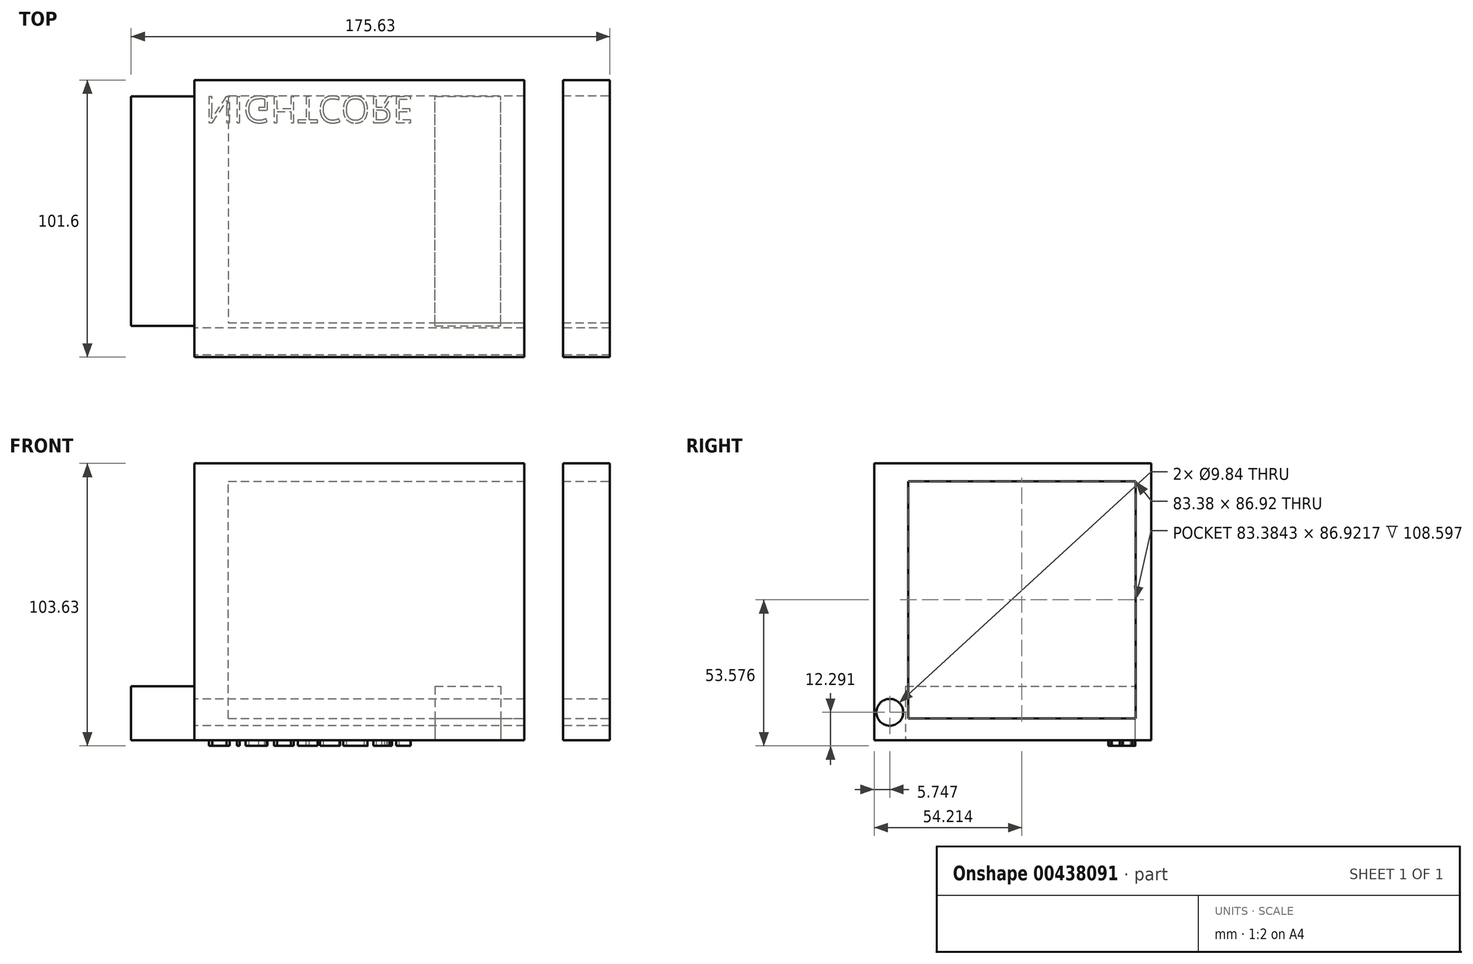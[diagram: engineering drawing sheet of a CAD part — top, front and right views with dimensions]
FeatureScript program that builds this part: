
annotation { "Feature Type Name" : "Feature", "Feature Type Description" : "" }
export const myFeature = defineFeature(function(context is Context, id is Id, definition is map)
    precondition{}
    {
        {
            var Q0;
            Q0=qCreatedBy(makeId("Top.planeOp"),FACE);
            var sketch = newSketch(context, id + "F0", { "sketchPlane" : qUnion([Q0])});
            skLineSegment(sketch, "E0.bottom", {"start": v(-70.16, 123.67) * mm, "end": v(82.24, 123.67) * mm});
            skLineSegment(sketch, "E0.top", {"start": v(-70.16, 22.07) * mm, "end": v(82.24, 22.07) * mm});
            skLineSegment(sketch, "E0.left", {"start": v(-70.16, 123.67) * mm, "end": v(-70.16, 22.07) * mm});
            skLineSegment(sketch, "E0.right", {"start": v(82.24, 123.67) * mm, "end": v(82.24, 22.07) * mm});
            skLineSegment(sketch, "E1.bottom", {"start": v(50.89, 123.67) * mm, "end": v(65.05, 123.67) * mm});
            skLineSegment(sketch, "E1.top", {"start": v(50.89, 22.07) * mm, "end": v(65.05, 22.07) * mm});
            skLineSegment(sketch, "E1.left", {"start": v(50.89, 123.67) * mm, "end": v(50.89, 22.07) * mm});
            skLineSegment(sketch, "E1.right", {"start": v(65.05, 123.67) * mm, "end": v(65.05, 22.07) * mm});
            skSolve(sketch);
        }
        {
            var Q0;
            {var subQ0=sQuery(id+"F0.wireOp",EDGE,"E0.right");Q0=makeQuery(id+"F0.imprint","IMPRINT",FACE,{"disambiguationData":[TD([[makeQuery(id+"F0.imprint","IMPRINT",EDGE,{"derivedFrom":subQ0}),-1.0]])]});}
            var Q1;
            {var subQ0=sQuery(id+"F0.wireOp",EDGE,"E0.left");Q1=makeQuery(id+"F0.imprint","IMPRINT",FACE,{"disambiguationData":[TD([[makeQuery(id+"F0.imprint","IMPRINT",EDGE,{"derivedFrom":subQ0}),1.0]])]});}
            var Q2;
            Q2=makeQuery(id+"F0.imprint","IMPRINT",FACE,{"disambiguationData":[TD([[makeQuery(id+"F0.imprint","IMPRINT",EDGE,{"derivedFrom":sQuery(id+"F0.wireOp",EDGE,"E1.bottom")}),-1.0]])]});
            extrude(context, id + "F1", {"entities" : qUnion([Q0, Q1, Q2]), "depth" : 101.6 * mm});
        }
        {
            var Q0;
            Q0=makeQuery(id+"F1.opExtrude","SWEPT_FACE",FACE,{"disambiguationData":[OSD([sQuery(id+"F0.wireOp",EDGE,"E0.left")])]});
            var sketch = newSketch(context, id + "F2", { "sketchPlane" : qUnion([Q0])});
            skCircle(sketch, "E2", {"center": v(-27.82, 10.26) * mm, "radius": 4.92 * mm});
            skSolve(sketch);
        }
        {
            var Q0;
            Q0=makeQuery(id+"F2.imprint","IMPRINT",FACE,{"disambiguationData":[TD([[makeQuery(id+"F2.imprint","IMPRINT",EDGE,{"derivedFrom":sQuery(id+"F2.wireOp",EDGE,"E2")}),1.0]])]});
            extrude(context, id + "F3", {"entities" : qUnion([Q0]), "operationType" : NewBodyOperationType.REMOVE, "oppositeDirection" : true, "depth" : 164.85 * mm});
        }
        {
            var Q0;
            Q0=makeQuery(id+"F1.opExtrude","CAP_FACE",FACE,{"disambiguationData":[OSD([sQuery(id+"F0.wireOp",EDGE,"E0.bottom"),sQuery(id+"F0.wireOp",EDGE,"E0.top"),sQuery(id+"F0.wireOp",EDGE,"E0.left"),sQuery(id+"F0.wireOp",EDGE,"E0.right"),sQuery(id+"F0.wireOp",EDGE,"E1.bottom"),sQuery(id+"F0.wireOp",EDGE,"E1.top")])],"isStart":true});
            var sketch = newSketch(context, id + "F4", { "sketchPlane" : qUnion([Q0])});
            skLineSegment(sketch, "E3.bottom", {"start": v(18.12, -33.55) * mm, "end": v(42.28, -33.55) * mm});
            skLineSegment(sketch, "E3.top", {"start": v(18.12, -117.72) * mm, "end": v(42.28, -117.72) * mm});
            skLineSegment(sketch, "E3.left", {"start": v(18.12, -33.55) * mm, "end": v(18.12, -117.72) * mm});
            skLineSegment(sketch, "E3.right", {"start": v(42.28, -33.55) * mm, "end": v(42.28, -117.72) * mm});
            skSolve(sketch);
        }
        {
            var Q0;
            Q0=makeQuery(id+"F4.imprint","IMPRINT",FACE,{"disambiguationData":[TD([[makeQuery(id+"F4.imprint","IMPRINT",EDGE,{"derivedFrom":sQuery(id+"F4.wireOp",EDGE,"E3.bottom")}),-1.0]])]});
            extrude(context, id + "F5", {"entities" : qUnion([Q0]), "operationType" : NewBodyOperationType.REMOVE, "oppositeDirection" : true, "depth" : 19.8 * mm});
        }
        {
            var Q0;
            Q0=makeQuery(id+"F1.opExtrude","CAP_FACE",FACE,{"disambiguationData":[OSD([sQuery(id+"F0.wireOp",EDGE,"E0.bottom"),sQuery(id+"F0.wireOp",EDGE,"E0.top"),sQuery(id+"F0.wireOp",EDGE,"E0.left"),sQuery(id+"F0.wireOp",EDGE,"E0.right"),sQuery(id+"F0.wireOp",EDGE,"E1.bottom"),sQuery(id+"F0.wireOp",EDGE,"E1.top")])],"isStart":true});
            var sketch = newSketch(context, id + "F6", { "sketchPlane" : qUnion([Q0])});
            skText(sketch, "E4", { "text": "NIGHTCORE", "fontName": "OpenSans-Regular.ttf"});
            const initialGuessF6  = {"E4": [-0.06612, -0.11772, 1, 0, 0.00973]};
            skSetInitialGuess(sketch, initialGuessF6);
            skSolve(sketch);
        }
        {
            var Q0;
            Q0 = qSketchRegion(id + "F6", true);
            extrude(context, id + "F7", {"entities" : qUnion([Q0]), "operationType" : NewBodyOperationType.ADD, "depth" : 2.03 * mm});
        }
        {
            var Q0;
            Q0=makeQuery(id+"F5.boolean.opBoolean","COPY",FACE,{"derivedFrom":makeQuery(id+"F5.opExtrude","SWEPT_FACE",FACE,{"disambiguationData":[OSD([sQuery(id+"F4.wireOp",EDGE,"E3.left")])]})});
            extrude(context, id + "F8", {"entities" : qUnion([Q0]), "operationType" : NewBodyOperationType.ADD, "oppositeDirection" : true, "depth" : 111.5 * mm});
        }
        {
            var Q0;
            Q0=makeQuery(id+"F1.opExtrude","SWEPT_FACE",FACE,{"disambiguationData":[OSD([sQuery(id+"F0.wireOp",EDGE,"E0.right")])]});
            var sketch = newSketch(context, id + "F9", { "sketchPlane" : qUnion([Q0])});
            skLineSegment(sketch, "E5.bottom", {"start": v(117.98, 8.09) * mm, "end": v(34.6, 8.09) * mm});
            skLineSegment(sketch, "E5.top", {"start": v(117.98, 95) * mm, "end": v(34.6, 95) * mm});
            skLineSegment(sketch, "E5.left", {"start": v(117.98, 8.09) * mm, "end": v(117.98, 95) * mm});
            skLineSegment(sketch, "E5.right", {"start": v(34.6, 8.09) * mm, "end": v(34.6, 95) * mm});
            skSolve(sketch);
        }
        {
            var Q0;
            Q0=makeQuery(id+"F9.imprint","IMPRINT",FACE,{"disambiguationData":[TD([[makeQuery(id+"F9.imprint","IMPRINT",EDGE,{"derivedFrom":sQuery(id+"F9.wireOp",EDGE,"E5.bottom")}),-1.0]])]});
            extrude(context, id + "F10", {"entities" : qUnion([Q0]), "operationType" : NewBodyOperationType.REMOVE, "oppositeDirection" : true, "depth" : 139.95 * mm});
        }
    });
